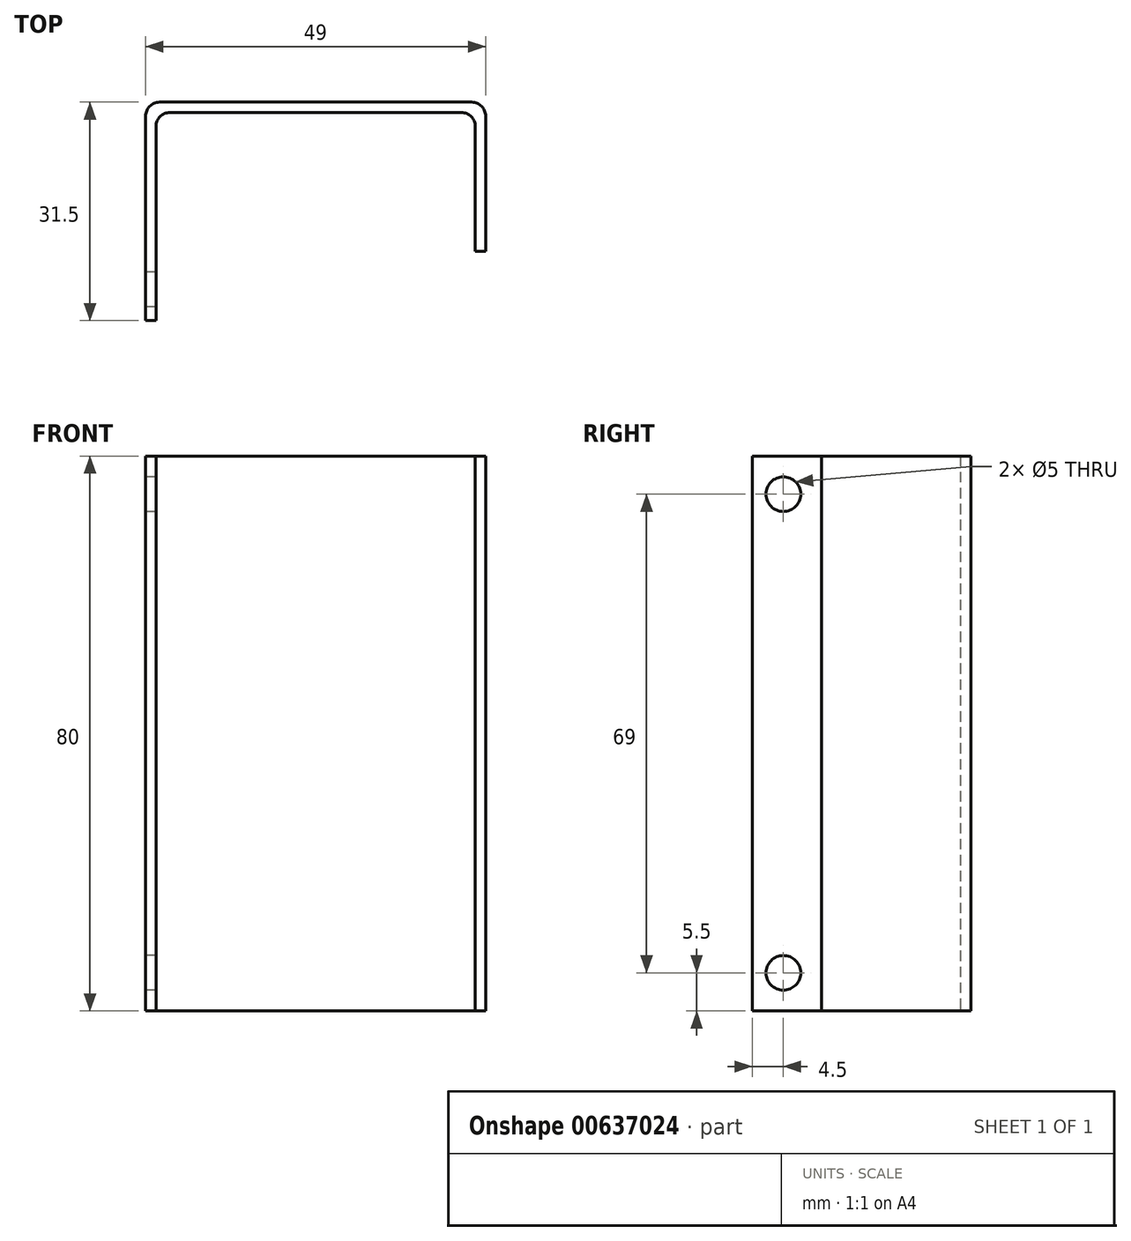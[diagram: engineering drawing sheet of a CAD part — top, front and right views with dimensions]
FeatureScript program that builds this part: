
annotation { "Feature Type Name" : "Feature", "Feature Type Description" : "" }
export const myFeature = defineFeature(function(context is Context, id is Id, definition is map)
    precondition{}
    {
        {
            var Q0;
            Q0=qCreatedBy(makeId("Top.planeOp"),FACE);
            var sketch = newSketch(context, id + "F0", { "sketchPlane" : qUnion([Q0])});
            skLineSegment(sketch, "E0", {"start": v(-2, 0) * mm, "end": v(-47, 0) * mm});
            skLineSegment(sketch, "E1", {"start": v(-49, -2) * mm, "end": v(-49, -31.5) * mm});
            skLineSegment(sketch, "E2", {"start": v(-49, -31.5) * mm, "end": v(-47.5, -31.5) * mm});
            skLineSegment(sketch, "E3", {"start": v(-47.5, -31.5) * mm, "end": v(-47.5, -3.5) * mm});
            skLineSegment(sketch, "E4", {"start": v(-45.5, -1.5) * mm, "end": v(-3.5, -1.5) * mm});
            skLineSegment(sketch, "E5", {"start": v(-1.5, -3.5) * mm, "end": v(-1.5, -21.5) * mm});
            skLineSegment(sketch, "E6", {"start": v(-1.5, -21.5) * mm, "end": v(0, -21.5) * mm});
            skLineSegment(sketch, "E7", {"start": v(0, -21.5) * mm, "end": v(0, -2) * mm});
            skPoint(sketch, "E8.visualSharp", {"position": v(-49, 0) * mm});
            skArc(sketch, "E8.filletArc", {"start": v(-47, 0) * mm, "mid": v(-48.41, -0.59) * mm, "end": v(-49, -2) * mm});
            skPoint(sketch, "E9.visualSharp", {"position": v(0, 0) * mm});
            skArc(sketch, "E9.filletArc", {"start": v(0, -2) * mm, "mid": v(-0.59, -0.59) * mm, "end": v(-2, 0) * mm});
            skPoint(sketch, "E10.visualSharp", {"position": v(-47.5, -1.5) * mm});
            skArc(sketch, "E10.filletArc", {"start": v(-45.5, -1.5) * mm, "mid": v(-46.91, -2.09) * mm, "end": v(-47.5, -3.5) * mm});
            skPoint(sketch, "E11.visualSharp", {"position": v(-1.5, -1.5) * mm});
            skArc(sketch, "E11.filletArc", {"start": v(-1.5, -3.5) * mm, "mid": v(-2.09, -2.09) * mm, "end": v(-3.5, -1.5) * mm});
            skSolve(sketch);
        }
        {
            var Q0;
            Q0=makeQuery(id+"F0.imprint","IMPRINT",FACE,{"disambiguationData":[TD([[makeQuery(id+"F0.imprint","IMPRINT",EDGE,{"derivedFrom":sQuery(id+"F0.wireOp",EDGE,"E0")}),1.0]])]});
            extrude(context, id + "F1", {"entities" : qUnion([Q0]), "depth" : 80 * mm, "offsetDistance" : 25 * mm});
        }
        {
            var Q0;
            Q0=makeQuery(id+"F1.opExtrude","SWEPT_FACE",FACE,{"disambiguationData":[OSD([sQuery(id+"F0.wireOp",EDGE,"E1")])]});
            var sketch = newSketch(context, id + "F2", { "sketchPlane" : qUnion([Q0])});
            skCircle(sketch, "E12", {"center": v(27, 5.5) * mm, "radius": 2.5 * mm});
            skCircle(sketch, "E13", {"center": v(27, 74.5) * mm, "radius": 2.5 * mm});
            skSolve(sketch);
        }
        {
            var Q0;
            Q0 = qSketchRegion(id + "F2", true);
            extrude(context, id + "F3", {"entities" : qUnion([Q0]), "operationType" : NewBodyOperationType.REMOVE, "endBound" : BoundingType.UP_TO_NEXT, "oppositeDirection" : true, "depth" : 25 * mm, "offsetDistance" : 25 * mm});
        }
    });
